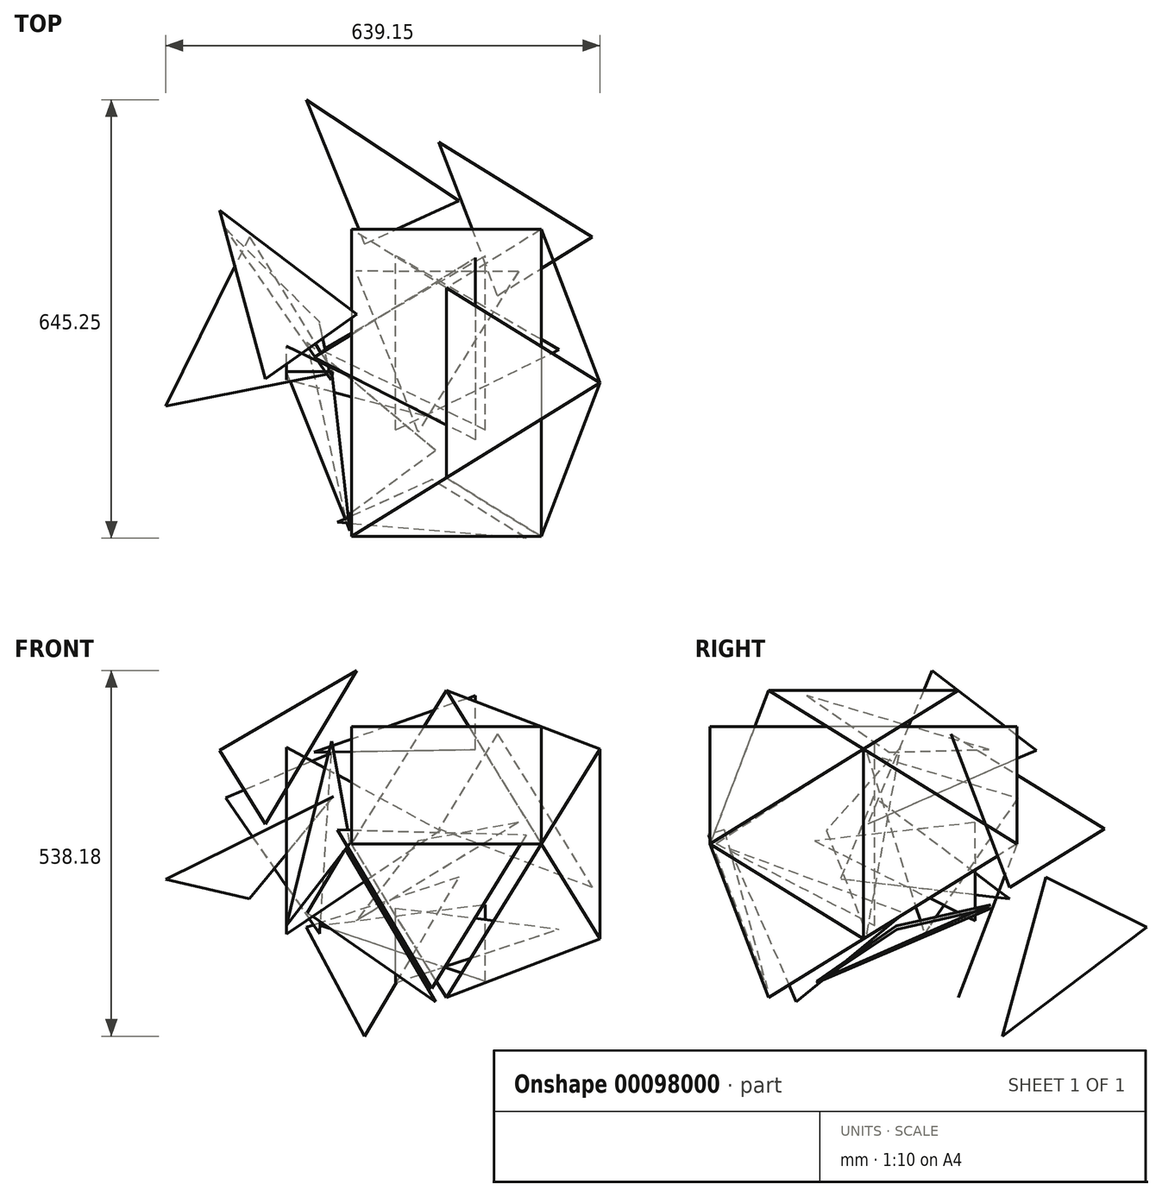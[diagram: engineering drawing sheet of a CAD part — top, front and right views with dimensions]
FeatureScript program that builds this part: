
annotation { "Feature Type Name" : "Feature", "Feature Type Description" : "" }
export const myFeature = defineFeature(function(context is Context, id is Id, definition is map)
    precondition{}
    {
        {
            var Q0;
            Q0=qCreatedBy(makeId("Top.planeOp"),FACE);
            var sketch = newSketch(context, id + "F0", { "sketchPlane" : qUnion([Q0])});
            skLineSegment(sketch, "E0.bottom", {"start": v(0, 0) * mm, "end": v(279.4, 0) * mm, "construction": true});
            skLineSegment(sketch, "E0.top", {"start": v(0, -279.4) * mm, "end": v(279.4, -279.4) * mm});
            skLineSegment(sketch, "E0.left", {"start": v(0, 0) * mm, "end": v(0, -279.4) * mm});
            skLineSegment(sketch, "E0.right", {"start": v(279.4, 0) * mm, "end": v(279.4, -279.4) * mm});
            skLineSegment(sketch, "E1", {"start": v(0, -139.7) * mm, "end": v(279.4, -139.7) * mm, "construction": true});
            skLineSegment(sketch, "E2", {"start": v(279.4, -139.7) * mm, "end": v(0, 0) * mm, "construction": true});
            skLineSegment(sketch, "E3", {"start": v(0, -139.7) * mm, "end": v(0, 172.68) * mm});
            skLineSegment(sketch, "E4", {"start": v(0, 172.68) * mm, "end": v(279.4, 172.68) * mm});
            skLineSegment(sketch, "E5", {"start": v(279.4, 172.68) * mm, "end": v(279.4, -139.7) * mm});
            skLineSegment(sketch, "E6", {"start": v(279.4, 99.77) * mm, "end": v(106.72, 99.77) * mm, "construction": true});
            skLineSegment(sketch, "E7", {"start": v(226.54, 0) * mm, "end": v(226.54, 172.68) * mm, "construction": true});
            skLineSegment(sketch, "E8", {"start": v(106.72, 0) * mm, "end": v(106.72, 172.68) * mm});
            skLineSegment(sketch, "E9.bottom", {"start": v(279.4, 0) * mm, "end": v(106.72, 0) * mm});
            skLineSegment(sketch, "E9.top", {"start": v(279.4, 172.68) * mm, "end": v(106.72, 172.68) * mm});
            skLineSegment(sketch, "E9.left", {"start": v(279.4, 0) * mm, "end": v(279.4, 172.68) * mm});
            skLineSegment(sketch, "E10", {"start": v(106.72, 33.15) * mm, "end": v(0, 33.15) * mm, "construction": true});
            skLineSegment(sketch, "E11", {"start": v(49.55, 172.68) * mm, "end": v(49.55, 65.96) * mm, "construction": true});
            skLineSegment(sketch, "E12.bottom", {"start": v(0, 172.68) * mm, "end": v(106.72, 172.68) * mm});
            skLineSegment(sketch, "E12.top", {"start": v(0, 65.96) * mm, "end": v(106.72, 65.96) * mm});
            skLineSegment(sketch, "E12.left", {"start": v(0, 172.68) * mm, "end": v(0, 65.96) * mm});
            skLineSegment(sketch, "E12.right", {"start": v(106.72, 172.68) * mm, "end": v(106.72, 65.96) * mm});
            skSolve(sketch);
        }
        {
            var Q0;
            Q0=qCreatedBy(makeId("Top.planeOp"),FACE);
            var sketch = newSketch(context, id + "F1", { "sketchPlane" : qUnion([Q0])});
            skPoint(sketch, "E13.0", {"position": v(0, 172.68) * mm});
            skPoint(sketch, "E14.0", {"position": v(279.4, -279.4) * mm});
            skLineSegment(sketch, "E15.bottom", {"start": v(0, 172.68) * mm, "end": v(279.4, 172.68) * mm});
            skLineSegment(sketch, "E15.top", {"start": v(0, -279.4) * mm, "end": v(279.4, -279.4) * mm});
            skLineSegment(sketch, "E15.left", {"start": v(0, 172.68) * mm, "end": v(0, -279.4) * mm});
            skLineSegment(sketch, "E15.right", {"start": v(279.4, 172.68) * mm, "end": v(279.4, -279.4) * mm});
            skLineSegment(sketch, "E16", {"start": v(0, -53.36) * mm, "end": v(279.4, -53.36) * mm, "construction": true});
            skLineSegment(sketch, "E17", {"start": v(139.7, 86.34) * mm, "end": v(139.7, -193.06) * mm});
            skPoint(sketch, "E17.startSnap0", {"position": v(139.7, -53.36) * mm});
            skSolve(sketch);
        }
        {
            var Q0;
            Q0 = qSketchRegion(id + "F1", true);
            extrude(context, id + "F2", {"entities" : qUnion([Q0]), "depth" : 172.67 * mm});
        }
        {
            var Q0;
            Q0=sQuery(id+"F1.wireOp",EDGE,"E17");
            var Q1;
            Q1=makeQuery(id+"F1.imprint","IMPRINT",FACE,{"disambiguationData":[TD([[makeQuery(id+"F1.imprint","IMPRINT",EDGE,{"derivedFrom":sQuery(id+"F1.wireOp",EDGE,"E15.bottom")}),-1.0]])]});
            cPlane(context, id + "F3", {"entities" : qUnion([Q0, Q1]), "cplaneType" : CPlaneType.LINE_ANGLE, "offset" : 152.4 * mm, "angle" : 90 * degree, "width" : 152.4 * mm, "height" : 152.4 * mm});
        }
        {
            var Q0;
            Q0=qCreatedBy(id+"F3.planeOp",FACE);
            var sketch = newSketch(context, id + "F4", { "sketchPlane" : qUnion([Q0])});
            skPoint(sketch, "E18.0", {"position": v(-53.36, 0) * mm});
            skLineSegment(sketch, "E19.0", {"start": v(86.34, 0) * mm, "end": v(-193.06, 0) * mm, "construction": true});
            skPoint(sketch, "E20.0", {"position": v(-193.06, 226.04) * mm});
            skPoint(sketch, "E21.0", {"position": v(86.34, -226.04) * mm});
            skLineSegment(sketch, "E22.bottom", {"start": v(-193.06, 226.04) * mm, "end": v(86.34, 226.04) * mm});
            skLineSegment(sketch, "E22.top", {"start": v(-193.06, -226.04) * mm, "end": v(86.34, -226.04) * mm});
            skLineSegment(sketch, "E22.left", {"start": v(-193.06, 226.04) * mm, "end": v(-193.06, -226.04) * mm});
            skLineSegment(sketch, "E22.right", {"start": v(86.34, 226.04) * mm, "end": v(86.34, -226.04) * mm});
            skLineSegment(sketch, "E23", {"start": v(-193.06, 0) * mm, "end": v(86.34, 0) * mm, "construction": true});
            skLineSegment(sketch, "E24", {"start": v(-53.36, 139.7) * mm, "end": v(-53.36, -139.7) * mm});
            skSolve(sketch);
        }
        {
            var Q0;
            Q0=sQuery(id+"F1.wireOp",EDGE,"E16");
            var Q1;
            Q1=makeQuery(id+"F1.imprint","IMPRINT",FACE,{"disambiguationData":[TD([[makeQuery(id+"F1.imprint","IMPRINT",EDGE,{"derivedFrom":sQuery(id+"F1.wireOp",EDGE,"E15.bottom")}),-1.0]])]});
            cPlane(context, id + "F5", {"entities" : qUnion([Q0, Q1]), "cplaneType" : CPlaneType.LINE_ANGLE, "offset" : 152.4 * mm, "angle" : 90 * degree, "width" : 152.4 * mm, "height" : 152.4 * mm});
        }
        {
            var Q0;
            Q0=qCreatedBy(id+"F5.planeOp",FACE);
            var sketch = newSketch(context, id + "F6", { "sketchPlane" : qUnion([Q0])});
            skPoint(sketch, "E25.0", {"position": v(0, 0) * mm});
            skPoint(sketch, "E26.0", {"position": v(-279.4, 0) * mm});
            skPoint(sketch, "E27.0", {"position": v(-139.7, 0) * mm});
            skLineSegment(sketch, "E28.bottom", {"start": v(86.34, -139.7) * mm, "end": v(-365.74, -139.7) * mm});
            skLineSegment(sketch, "E28.top", {"start": v(86.34, 139.7) * mm, "end": v(-365.74, 139.7) * mm});
            skLineSegment(sketch, "E28.left", {"start": v(86.34, -139.7) * mm, "end": v(86.34, 139.7) * mm});
            skLineSegment(sketch, "E28.right", {"start": v(-365.74, -139.7) * mm, "end": v(-365.74, 139.7) * mm});
            skLineSegment(sketch, "E29", {"start": v(-139.7, 139.7) * mm, "end": v(-139.7, 0) * mm, "construction": true});
            skLineSegment(sketch, "E30.0", {"start": v(0, 0) * mm, "end": v(-279.4, 0) * mm});
            skLineSegment(sketch, "E31.0", {"start": v(-139.7, 226.04) * mm, "end": v(-139.7, -226.04) * mm, "construction": true});
            skSolve(sketch);
        }
        {
            var Q0;
            Q0=sQuery(id+"F4.wireOp",VERTEX,"E20.0");
            var Q1;
            Q1=sQuery(id+"F6.wireOp",VERTEX,"E28.right.end");
            var Q2;
            Q2=sQuery(id+"F1.wireOp",VERTEX,"E14.0");
            cPlane(context, id + "F7", {"entities" : qUnion([Q0, Q1, Q2]), "cplaneType" : CPlaneType.THREE_POINT, "offset" : 152.4 * mm, "width" : 152.4 * mm, "height" : 152.4 * mm});
        }
        {
            var Q0;
            Q0=qCreatedBy(id+"F7.planeOp",FACE);
            var sketch = newSketch(context, id + "F8", { "sketchPlane" : qUnion([Q0])});
            skPoint(sketch, "E32.0", {"position": v(-57.03, 23.32) * mm});
            skPoint(sketch, "E33.0", {"position": v(114.06, -197.57) * mm});
            skPoint(sketch, "E34.0", {"position": v(219.8, 61.05) * mm});
            skLineSegment(sketch, "E35", {"start": v(-57.03, 23.32) * mm, "end": v(219.8, 61.05) * mm});
            skLineSegment(sketch, "E36", {"start": v(114.06, -197.57) * mm, "end": v(219.8, 61.05) * mm});
            skLineSegment(sketch, "E37", {"start": v(-57.03, 23.32) * mm, "end": v(114.06, -197.57) * mm});
            skSolve(sketch);
        }
        {
            var Q0;
            Q0=sQuery(id+"F1.wireOp",VERTEX,"E14.0");
            var Q1;
            Q1=sQuery(id+"F6.wireOp",VERTEX,"E28.right.start");
            var Q2;
            Q2=sQuery(id+"F8.wireOp",VERTEX,"E34.0");
            cPlane(context, id + "F9", {"entities" : qUnion([Q0, Q1, Q2]), "cplaneType" : CPlaneType.THREE_POINT, "offset" : 152.4 * mm, "width" : 152.4 * mm, "height" : 152.4 * mm});
        }
        {
            var Q0;
            Q0=qCreatedBy(id+"F9.planeOp",FACE);
            var sketch = newSketch(context, id + "F10", { "sketchPlane" : qUnion([Q0])});
            skPoint(sketch, "E38.0", {"position": v(-80.66, 139.7) * mm});
            skPoint(sketch, "E39.0", {"position": v(-80.66, -139.7) * mm});
            skPoint(sketch, "E40.0", {"position": v(161.31, 0) * mm});
            skLineSegment(sketch, "E41", {"start": v(161.31, 0) * mm, "end": v(-80.66, -139.7) * mm});
            skLineSegment(sketch, "E42", {"start": v(-80.66, -139.7) * mm, "end": v(-80.66, 139.7) * mm});
            skLineSegment(sketch, "E43.0", {"start": v(161.31, 0) * mm, "end": v(-80.66, 139.7) * mm});
            skSolve(sketch);
        }
        {
            var Q0;
            Q0=sQuery(id+"F4.wireOp",VERTEX,"E22.left.end");
            var Q1;
            Q1=sQuery(id+"F10.wireOp",VERTEX,"E40.0");
            var Q2;
            Q2=sQuery(id+"F10.wireOp",VERTEX,"E39.0");
            cPlane(context, id + "F11", {"entities" : qUnion([Q0, Q1, Q2]), "cplaneType" : CPlaneType.THREE_POINT, "offset" : 152.4 * mm, "width" : 152.4 * mm, "height" : 152.4 * mm});
        }
        {
            var Q0;
            Q0=qCreatedBy(id+"F11.planeOp",FACE);
            var sketch = newSketch(context, id + "F12", { "sketchPlane" : qUnion([Q0])});
            skPoint(sketch, "E44.0", {"position": v(114.06, 197.57) * mm});
            skPoint(sketch, "E45.0", {"position": v(-57.03, -23.32) * mm});
            skPoint(sketch, "E46.0", {"position": v(219.8, -61.05) * mm});
            skLineSegment(sketch, "E47", {"start": v(114.06, 197.57) * mm, "end": v(-57.03, -23.32) * mm});
            skLineSegment(sketch, "E48", {"start": v(-57.03, -23.32) * mm, "end": v(219.8, -61.05) * mm});
            skLineSegment(sketch, "E49", {"start": v(219.8, -61.05) * mm, "end": v(114.06, 197.57) * mm});
            skSolve(sketch);
        }
        {
            var Q0;
            Q0=sQuery(id+"F10.wireOp",VERTEX,"E40.0");
            var Q1;
            Q1=sQuery(id+"F1.wireOp",VERTEX,"E15.left.end");
            var Q2;
            Q2=sQuery(id+"F8.wireOp",VERTEX,"E32.0");
            cPlane(context, id + "F13", {"entities" : qUnion([Q0, Q1, Q2]), "cplaneType" : CPlaneType.THREE_POINT, "offset" : 152.4 * mm, "width" : 152.4 * mm, "height" : 152.4 * mm});
        }
        {
            var Q0;
            Q0=qCreatedBy(id+"F13.planeOp",FACE);
            var sketch = newSketch(context, id + "F14", { "sketchPlane" : qUnion([Q0])});
            skLineSegment(sketch, "E50.0", {"start": v(0, -99.7) * mm, "end": v(279.4, -99.7) * mm});
            skLineSegment(sketch, "E51.0", {"start": v(139.7, 142.27) * mm, "end": v(279.4, -99.7) * mm});
            skLineSegment(sketch, "E52", {"start": v(139.7, 142.27) * mm, "end": v(0, -99.7) * mm});
            skSolve(sketch);
        }
        {
            var Q0;
            Q0=sQuery(id+"F1.wireOp",VERTEX,"E15.right.start");
            var Q1;
            Q1=sQuery(id+"F4.wireOp",VERTEX,"E22.right.start");
            var Q2;
            Q2=sQuery(id+"F10.wireOp",VERTEX,"E38.0");
            cPlane(context, id + "F15", {"entities" : qUnion([Q0, Q1, Q2]), "cplaneType" : CPlaneType.THREE_POINT, "offset" : 152.4 * mm, "width" : 152.4 * mm, "height" : 152.4 * mm});
        }
        {
            var Q0;
            Q0=qCreatedBy(id+"F15.planeOp",FACE);
            var sketch = newSketch(context, id + "F16", { "sketchPlane" : qUnion([Q0])});
            skPoint(sketch, "E53.0", {"position": v(249.91, -159.83) * mm});
            skPoint(sketch, "E54.0", {"position": v(78.82, 61.05) * mm});
            skPoint(sketch, "E55.0", {"position": v(-26.93, -197.57) * mm});
            skLineSegment(sketch, "E56", {"start": v(78.82, 61.05) * mm, "end": v(249.91, -159.83) * mm});
            skLineSegment(sketch, "E57", {"start": v(249.91, -159.83) * mm, "end": v(-26.93, -197.57) * mm});
            skLineSegment(sketch, "E58", {"start": v(78.82, 61.05) * mm, "end": v(-26.93, -197.57) * mm});
            skSolve(sketch);
        }
        {
            var Q0;
            Q0=sQuery(id+"F8.wireOp",VERTEX,"E32.0");
            var Q1;
            Q1=sQuery(id+"F4.wireOp",VERTEX,"E22.right.start");
            var Q2;
            Q2=sQuery(id+"F10.wireOp",VERTEX,"E38.0");
            cPlane(context, id + "F17", {"entities" : qUnion([Q0, Q1, Q2]), "cplaneType" : CPlaneType.THREE_POINT, "offset" : 152.4 * mm, "width" : 152.4 * mm, "height" : 152.4 * mm});
        }
        {
            var Q0;
            Q0=qCreatedBy(id+"F17.planeOp",FACE);
            var sketch = newSketch(context, id + "F18", { "sketchPlane" : qUnion([Q0])});
            skLineSegment(sketch, "E59.0", {"start": v(49.85, -193.06) * mm, "end": v(49.85, 86.34) * mm});
            skLineSegment(sketch, "E60.0", {"start": v(49.85, 86.34) * mm, "end": v(291.82, -53.36) * mm});
            skLineSegment(sketch, "E61.0", {"start": v(49.85, -193.06) * mm, "end": v(291.82, -53.36) * mm});
            skSolve(sketch);
        }
        {
            var Q0;
            Q0=sQuery(id+"F10.wireOp",VERTEX,"E39.0");
            var Q1;
            Q1=sQuery(id+"F10.wireOp",VERTEX,"E38.0");
            var Q2;
            Q2=sQuery(id+"F1.wireOp",VERTEX,"E15.right.start");
            cPlane(context, id + "F19", {"entities" : qUnion([Q0, Q1, Q2]), "cplaneType" : CPlaneType.THREE_POINT, "offset" : 152.4 * mm, "width" : 152.4 * mm, "height" : 152.4 * mm});
        }
        {
            var Q0;
            Q0=qCreatedBy(id+"F19.planeOp",FACE);
            var sketch = newSketch(context, id + "F20", { "sketchPlane" : qUnion([Q0])});
            skLineSegment(sketch, "E62.0", {"start": v(-180.35, 139.7) * mm, "end": v(61.62, 0) * mm});
            skLineSegment(sketch, "E63.0", {"start": v(-180.35, -139.7) * mm, "end": v(-180.35, 139.7) * mm});
            skLineSegment(sketch, "E64", {"start": v(61.62, 0) * mm, "end": v(-180.35, -139.7) * mm});
            skSolve(sketch);
        }
        {
            var Q0;
            Q0=sQuery(id+"F16.wireOp",VERTEX,"E55.0");
            var Q1;
            Q1=sQuery(id+"F16.wireOp",VERTEX,"E54.0");
            var Q2;
            Q2=sQuery(id+"F1.wireOp",VERTEX,"E13.0");
            cPlane(context, id + "F21", {"entities" : qUnion([Q0, Q1, Q2]), "cplaneType" : CPlaneType.THREE_POINT, "offset" : 152.4 * mm, "width" : 152.4 * mm, "height" : 152.4 * mm});
        }
        {
            var Q0;
            Q0=qCreatedBy(id+"F21.planeOp",FACE);
            var sketch = newSketch(context, id + "F22", { "sketchPlane" : qUnion([Q0])});
            skLineSegment(sketch, "E65.0", {"start": v(0, -61.62) * mm, "end": v(-279.4, -61.62) * mm});
            skLineSegment(sketch, "E66.0", {"start": v(-139.7, 180.35) * mm, "end": v(-279.4, -61.62) * mm});
            skLineSegment(sketch, "E67", {"start": v(-139.7, 180.35) * mm, "end": v(0, -61.62) * mm});
            skSolve(sketch);
        }
        {
            var Q0;
            Q0=sQuery(id+"F16.wireOp",VERTEX,"E54.0");
            var Q1;
            Q1=sQuery(id+"F6.wireOp",VERTEX,"E28.left.end");
            var Q2;
            Q2=sQuery(id+"F8.wireOp",VERTEX,"E32.0");
            cPlane(context, id + "F23", {"entities" : qUnion([Q0, Q1, Q2]), "cplaneType" : CPlaneType.THREE_POINT, "offset" : 152.4 * mm, "width" : 152.4 * mm, "height" : 152.4 * mm});
        }
        {
            var Q0;
            Q0=qCreatedBy(id+"F23.planeOp",FACE);
            var sketch = newSketch(context, id + "F24", { "sketchPlane" : qUnion([Q0])});
            skPoint(sketch, "E68.0", {"position": v(211.16, -86.34) * mm});
            skPoint(sketch, "E69.0", {"position": v(-30.8, 53.36) * mm});
            skPoint(sketch, "E70.0", {"position": v(211.16, 193.06) * mm});
            skLineSegment(sketch, "E71", {"start": v(211.16, -86.34) * mm, "end": v(211.16, 193.06) * mm});
            skLineSegment(sketch, "E72", {"start": v(211.16, 193.06) * mm, "end": v(-30.8, 53.36) * mm});
            skLineSegment(sketch, "E73", {"start": v(-30.8, 53.36) * mm, "end": v(211.16, -86.34) * mm});
            skSolve(sketch);
        }
        {
            var Q0;
            Q0=sQuery(id+"F16.wireOp",VERTEX,"E55.0");
            var Q1;
            Q1=sQuery(id+"F4.wireOp",VERTEX,"E21.0");
            var Q2;
            Q2=sQuery(id+"F10.wireOp",VERTEX,"E39.0");
            cPlane(context, id + "F25", {"entities" : qUnion([Q0, Q1, Q2]), "cplaneType" : CPlaneType.THREE_POINT, "offset" : 152.4 * mm, "width" : 152.4 * mm, "height" : 152.4 * mm});
        }
        {
            var Q0;
            Q0=qCreatedBy(id+"F25.planeOp",FACE);
            var sketch = newSketch(context, id + "F26", { "sketchPlane" : qUnion([Q0])});
            skPoint(sketch, "E74.0", {"position": v(157.63, -122.1) * mm});
            skPoint(sketch, "E75.0", {"position": v(263.38, 136.51) * mm});
            skPoint(sketch, "E76.0", {"position": v(-13.46, 98.78) * mm});
            skLineSegment(sketch, "E77.0", {"start": v(157.63, -122.1) * mm, "end": v(263.38, 136.51) * mm});
            skLineSegment(sketch, "E78", {"start": v(157.63, -122.1) * mm, "end": v(-13.46, 98.78) * mm});
            skLineSegment(sketch, "E79", {"start": v(-13.46, 98.78) * mm, "end": v(263.38, 136.51) * mm});
            skSolve(sketch);
        }
        {
            var Q0;
            Q0=sQuery(id+"F22.wireOp",VERTEX,"E67.end");
            var Q1;
            Q1=sQuery(id+"F24.wireOp",VERTEX,"E69.0");
            var Q2;
            Q2=sQuery(id+"F6.wireOp",VERTEX,"E28.left.start");
            cPlane(context, id + "F27", {"entities" : qUnion([Q0, Q1, Q2]), "cplaneType" : CPlaneType.THREE_POINT, "offset" : 152.4 * mm, "width" : 152.4 * mm, "height" : 152.4 * mm});
        }
        {
            var Q0;
            Q0=qCreatedBy(id+"F27.planeOp",FACE);
            var sketch = newSketch(context, id + "F28", { "sketchPlane" : qUnion([Q0])});
            skPoint(sketch, "E80.0", {"position": v(-161.31, 0) * mm});
            skPoint(sketch, "E81.0", {"position": v(80.66, 139.7) * mm});
            skPoint(sketch, "E82.0", {"position": v(80.66, -139.7) * mm});
            skLineSegment(sketch, "E83", {"start": v(-161.31, 0) * mm, "end": v(80.66, -139.7) * mm});
            skLineSegment(sketch, "E84", {"start": v(80.66, -139.7) * mm, "end": v(80.66, 139.7) * mm});
            skLineSegment(sketch, "E85", {"start": v(80.66, 139.7) * mm, "end": v(-161.31, 0) * mm});
            skSolve(sketch);
        }
        {
            var Q0;
            Q0=sQuery(id+"F20.wireOp",VERTEX,"E62.0.end");
            var Q1;
            Q1=sQuery(id+"F4.wireOp",VERTEX,"E21.0");
            var Q2;
            Q2=sQuery(id+"F1.wireOp",VERTEX,"E13.0");
            cPlane(context, id + "F29", {"entities" : qUnion([Q0, Q1, Q2]), "cplaneType" : CPlaneType.THREE_POINT, "offset" : 152.4 * mm, "width" : 152.4 * mm, "height" : 152.4 * mm});
        }
        {
            var Q0;
            Q0=qCreatedBy(id+"F29.planeOp",FACE);
            var sketch = newSketch(context, id + "F30", { "sketchPlane" : qUnion([Q0])});
            skLineSegment(sketch, "E86.0", {"start": v(0, 61.62) * mm, "end": v(279.4, 61.62) * mm});
            skLineSegment(sketch, "E87.0", {"start": v(279.4, 61.62) * mm, "end": v(139.7, -180.35) * mm});
            skLineSegment(sketch, "E88", {"start": v(139.7, -180.35) * mm, "end": v(0, 61.62) * mm});
            skSolve(sketch);
        }
        {
            var Q0;
            Q0=sQuery(id+"F22.wireOp",VERTEX,"E67.end");
            var Q1;
            Q1=sQuery(id+"F24.wireOp",VERTEX,"E69.0");
            var Q2;
            Q2=sQuery(id+"F22.wireOp",VERTEX,"E67.start");
            cPlane(context, id + "F31", {"entities" : qUnion([Q0, Q1, Q2]), "cplaneType" : CPlaneType.THREE_POINT, "offset" : 152.4 * mm, "width" : 152.4 * mm, "height" : 152.4 * mm});
        }
        {
            var Q0;
            Q0=qCreatedBy(id+"F31.planeOp",FACE);
            var sketch = newSketch(context, id + "F32", { "sketchPlane" : qUnion([Q0])});
            skLineSegment(sketch, "E89.0", {"start": v(-35.25, 136.51) * mm, "end": v(70.5, -122.1) * mm});
            skLineSegment(sketch, "E90.0", {"start": v(-35.25, 136.51) * mm, "end": v(241.6, 98.78) * mm});
            skLineSegment(sketch, "E91.0", {"start": v(241.6, 98.78) * mm, "end": v(70.5, -122.1) * mm});
            skSolve(sketch);
        }
        {
            var Q0;
            Q0=sQuery(id+"F28.wireOp",VERTEX,"E80.0");
            var Q1;
            Q1=sQuery(id+"F26.wireOp",VERTEX,"E79.start");
            var Q2;
            Q2=sQuery(id+"F28.wireOp",VERTEX,"E82.0");
            cPlane(context, id + "F33", {"entities" : qUnion([Q0, Q1, Q2]), "cplaneType" : CPlaneType.THREE_POINT, "offset" : 152.4 * mm, "width" : 152.4 * mm, "height" : 152.4 * mm});
        }
        {
            var Q0;
            Q0=qCreatedBy(id+"F33.planeOp",FACE);
            var sketch = newSketch(context, id + "F34", { "sketchPlane" : qUnion([Q0])});
            skLineSegment(sketch, "E92.0", {"start": v(70.5, 122.1) * mm, "end": v(-35.25, -136.51) * mm});
            skLineSegment(sketch, "E93.0", {"start": v(241.6, -98.78) * mm, "end": v(70.5, 122.1) * mm});
            skLineSegment(sketch, "E94", {"start": v(241.6, -98.78) * mm, "end": v(-35.25, -136.51) * mm});
            skSolve(sketch);
        }
        {
            var Q0;
            Q0=sQuery(id+"F28.wireOp",VERTEX,"E82.0");
            var Q1;
            Q1=sQuery(id+"F26.wireOp",VERTEX,"E76.0");
            var Q2;
            Q2=sQuery(id+"F12.wireOp",VERTEX,"E45.0");
            cPlane(context, id + "F35", {"entities" : qUnion([Q0, Q1, Q2]), "cplaneType" : CPlaneType.THREE_POINT, "offset" : 152.4 * mm, "width" : 152.4 * mm, "height" : 152.4 * mm});
        }
        {
            var Q0;
            Q0=qCreatedBy(id+"F35.planeOp",FACE);
            var sketch = newSketch(context, id + "F36", { "sketchPlane" : qUnion([Q0])});
            skLineSegment(sketch, "E95.0", {"start": v(211.16, 86.34) * mm, "end": v(-30.8, -53.36) * mm});
            skPoint(sketch, "E96.0", {"position": v(211.16, -193.06) * mm});
            skLineSegment(sketch, "E97", {"start": v(-30.8, -53.36) * mm, "end": v(211.16, -193.06) * mm});
            skLineSegment(sketch, "E98", {"start": v(211.16, -193.06) * mm, "end": v(211.16, 86.34) * mm});
            skSolve(sketch);
        }
        {
            var Q0;
            Q0=sQuery(id+"F12.wireOp",VERTEX,"E45.0");
            var Q1;
            Q1=sQuery(id+"F10.wireOp",VERTEX,"E39.0");
            var Q2;
            Q2=sQuery(id+"F26.wireOp",VERTEX,"E76.0");
            cPlane(context, id + "F37", {"entities" : qUnion([Q0, Q1, Q2]), "cplaneType" : CPlaneType.THREE_POINT, "offset" : 152.4 * mm, "width" : 152.4 * mm, "height" : 152.4 * mm});
        }
        {
            var Q0;
            Q0=qCreatedBy(id+"F37.planeOp",FACE);
            var sketch = newSketch(context, id + "F38", { "sketchPlane" : qUnion([Q0])});
            skLineSegment(sketch, "E99.0", {"start": v(49.85, 193.06) * mm, "end": v(49.85, -86.34) * mm});
            skLineSegment(sketch, "E100.0", {"start": v(49.85, -86.34) * mm, "end": v(291.82, 53.36) * mm});
            skLineSegment(sketch, "E101.0", {"start": v(49.85, 193.06) * mm, "end": v(291.82, 53.36) * mm});
            skSolve(sketch);
        }
        {
            var Q0;
            Q0=sQuery(id+"F24.wireOp",VERTEX,"E69.0");
            var Q1;
            Q1=sQuery(id+"F14.wireOp",VERTEX,"E52.end");
            var Q2;
            Q2=sQuery(id+"F8.wireOp",VERTEX,"E32.0");
            cPlane(context, id + "F39", {"entities" : qUnion([Q0, Q1, Q2]), "cplaneType" : CPlaneType.THREE_POINT, "offset" : 152.4 * mm, "width" : 152.4 * mm, "height" : 152.4 * mm});
        }
        {
            var Q0;
            Q0=qCreatedBy(id+"F39.planeOp",FACE);
            var sketch = newSketch(context, id + "F40", { "sketchPlane" : qUnion([Q0])});
            skLineSegment(sketch, "E102.0", {"start": v(285.16, -23.32) * mm, "end": v(8.32, -61.05) * mm});
            skLineSegment(sketch, "E103.0", {"start": v(285.16, -23.32) * mm, "end": v(114.06, 197.57) * mm});
            skLineSegment(sketch, "E104", {"start": v(114.06, 197.57) * mm, "end": v(8.32, -61.05) * mm});
            skSolve(sketch);
        }
        {
            var Q0;
            Q0=sQuery(id+"F32.wireOp",VERTEX,"E90.0.start");
            var Q1;
            Q1=sQuery(id+"F14.wireOp",VERTEX,"E52.end");
            var Q2;
            Q2=sQuery(id+"F28.wireOp",VERTEX,"E82.0");
            cPlane(context, id + "F41", {"entities" : qUnion([Q0, Q1, Q2]), "cplaneType" : CPlaneType.THREE_POINT, "offset" : 152.4 * mm, "width" : 152.4 * mm, "height" : 152.4 * mm});
        }
        {
            var Q0;
            Q0=qCreatedBy(id+"F41.planeOp",FACE);
            var sketch = newSketch(context, id + "F42", { "sketchPlane" : qUnion([Q0])});
            skLineSegment(sketch, "E105.0", {"start": v(19.04, -139.7) * mm, "end": v(19.04, 139.7) * mm});
            skLineSegment(sketch, "E106.0", {"start": v(261, 0) * mm, "end": v(19.04, 139.7) * mm});
            skLineSegment(sketch, "E107", {"start": v(261, 0) * mm, "end": v(19.04, -139.7) * mm});
            skSolve(sketch);
        }
        {
            var Q0;
            Q0=sQuery(id+"F14.wireOp",VERTEX,"E52.end");
            var Q1;
            Q1=sQuery(id+"F12.wireOp",VERTEX,"E48.start");
            var Q2;
            Q2=sQuery(id+"F36.wireOp",VERTEX,"E95.0.end");
            cPlane(context, id + "F43", {"entities" : qUnion([Q0, Q1, Q2]), "cplaneType" : CPlaneType.THREE_POINT, "offset" : 152.4 * mm, "width" : 152.4 * mm, "height" : 152.4 * mm});
        }
        {
            var Q0;
            Q0=qCreatedBy(id+"F43.planeOp",FACE);
            var sketch = newSketch(context, id + "F44", { "sketchPlane" : qUnion([Q0])});
            skLineSegment(sketch, "E108.0", {"start": v(228.13, 0) * mm, "end": v(-48.71, -37.73) * mm});
            skLineSegment(sketch, "E109.0", {"start": v(-48.71, -37.73) * mm, "end": v(122.39, -258.62) * mm});
            skLineSegment(sketch, "E110", {"start": v(228.13, 0) * mm, "end": v(122.39, -258.62) * mm});
            skSolve(sketch);
        }
        {
            var Q0;
            Q0=sQuery(id+"F44.wireOp",VERTEX,"E110.start");
            var Q1;
            Q1=sQuery(id+"F12.wireOp",VERTEX,"E45.0");
            var Q2;
            Q2=sQuery(id+"F10.wireOp",VERTEX,"E40.0");
            cPlane(context, id + "F45", {"entities" : qUnion([Q0, Q1, Q2]), "cplaneType" : CPlaneType.THREE_POINT, "offset" : 152.4 * mm, "width" : 152.4 * mm, "height" : 152.4 * mm});
        }
        {
            var Q0;
            Q0=qCreatedBy(id+"F45.planeOp",FACE);
            var sketch = newSketch(context, id + "F46", { "sketchPlane" : qUnion([Q0])});
            skLineSegment(sketch, "E111.0", {"start": v(0, 99.7) * mm, "end": v(-279.4, 99.7) * mm});
            skLineSegment(sketch, "E112.0", {"start": v(0, 99.7) * mm, "end": v(-139.7, -142.27) * mm});
            skLineSegment(sketch, "E113.0", {"start": v(-279.4, 99.7) * mm, "end": v(-139.7, -142.27) * mm});
            skSolve(sketch);
        }
        {
            var Q0;
            Q0 = qSketchRegion(id + "F46", true);
            var Q1;
            Q1=makeQuery(id+"F14.imprint","IMPRINT",FACE,{"disambiguationData":[TD([[makeQuery(id+"F14.imprint","IMPRINT",EDGE,{"derivedFrom":sQuery(id+"F14.wireOp",EDGE,"E50.0")}),1.0]])]});
            var Q2;
            Q2=makeQuery(id+"F44.imprint","IMPRINT",FACE,{"disambiguationData":[TD([[makeQuery(id+"F44.imprint","IMPRINT",EDGE,{"derivedFrom":sQuery(id+"F44.wireOp",EDGE,"E108.0")}),1.0]])]});
            var Q3;
            Q3=makeQuery(id+"F42.imprint","IMPRINT",FACE,{"disambiguationData":[TD([[makeQuery(id+"F42.imprint","IMPRINT",EDGE,{"derivedFrom":sQuery(id+"F42.wireOp",EDGE,"E105.0")}),-1.0]])]});
            var Q4;
            Q4=makeQuery(id+"F40.imprint","IMPRINT",FACE,{"disambiguationData":[TD([[makeQuery(id+"F40.imprint","IMPRINT",EDGE,{"derivedFrom":sQuery(id+"F40.wireOp",EDGE,"E102.0")}),-1.0]])]});
            var Q5;
            Q5=makeQuery(id+"F12.imprint","IMPRINT",FACE,{"disambiguationData":[TD([[makeQuery(id+"F12.imprint","IMPRINT",EDGE,{"derivedFrom":sQuery(id+"F12.wireOp",EDGE,"E47")}),1.0]])]});
            var Q6;
            Q6 = qSketchRegion(id + "F38", true);
            var Q7;
            Q7 = qSketchRegion(id + "F36", true);
            var Q8;
            Q8 = qSketchRegion(id + "F34", true);
            var Q9;
            Q9 = qSketchRegion(id + "F32", true);
            var Q10;
            Q10 = qSketchRegion(id + "F30", true);
            var Q11;
            Q11 = qSketchRegion(id + "F28", true);
            var Q12;
            Q12 = qSketchRegion(id + "F26", true);
            var Q13;
            Q13 = qSketchRegion(id + "F24", true);
            var Q14;
            Q14 = qSketchRegion(id + "F22", true);
            var Q15;
            Q15 = qSketchRegion(id + "F20", true);
            var Q16;
            Q16 = qSketchRegion(id + "F18", true);
            var Q17;
            Q17 = qSketchRegion(id + "F16", true);
            var Q18;
            Q18 = qSketchRegion(id + "F10", true);
            var Q19;
            Q19 = qSketchRegion(id + "F8", true);
            extrude(context, id + "F47", {"entities" : qUnion([Q0, Q1, Q2, Q3, Q4, Q5, Q6, Q7, Q8, Q9, Q10, Q11, Q12, Q13, Q14, Q15, Q16, Q17, Q18, Q19]), "depth" : 0.01 * mm});
        }
    });
